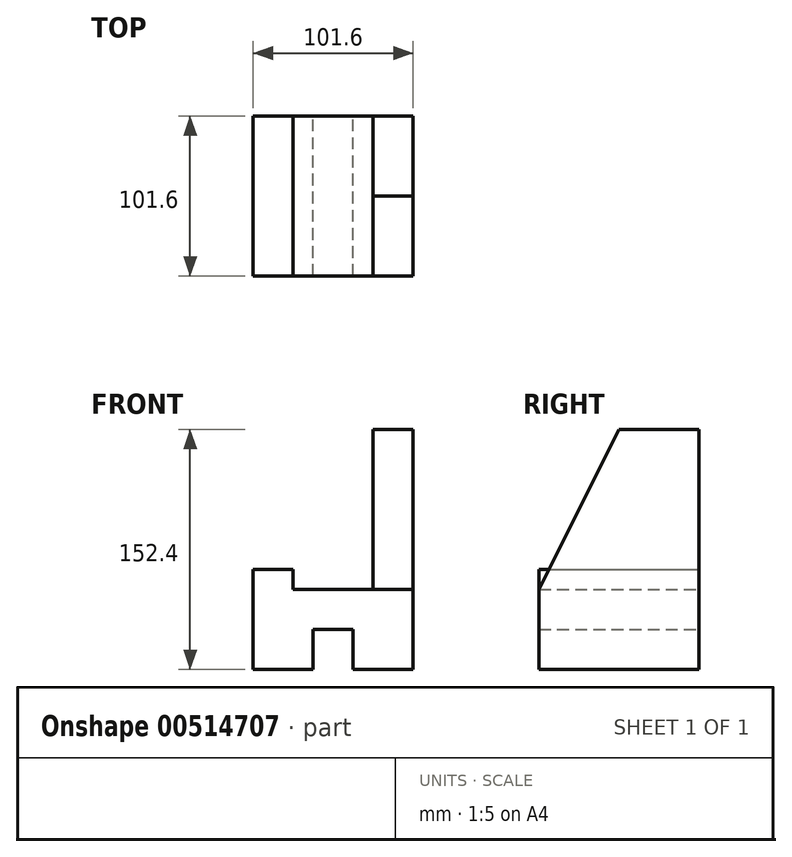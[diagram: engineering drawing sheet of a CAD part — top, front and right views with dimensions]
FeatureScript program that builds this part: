
annotation { "Feature Type Name" : "Feature", "Feature Type Description" : "" }
export const myFeature = defineFeature(function(context is Context, id is Id, definition is map)
    precondition{}
    {
        {
            var Q0;
            Q0=qCreatedBy(makeId("Front.planeOp"),FACE);
            var sketch = newSketch(context, id + "F0", { "sketchPlane" : qUnion([Q0])});
            skLineSegment(sketch, "E0", {"start": v(0, 0) * mm, "end": v(-76.2, 0) * mm});
            skLineSegment(sketch, "E1", {"start": v(-76.2, 0) * mm, "end": v(-76.2, 12.7) * mm});
            skLineSegment(sketch, "E2", {"start": v(-76.2, 12.7) * mm, "end": v(-101.6, 12.7) * mm});
            skLineSegment(sketch, "E3", {"start": v(-101.6, 12.7) * mm, "end": v(-101.6, -50.8) * mm});
            skLineSegment(sketch, "E4", {"start": v(-101.6, -50.8) * mm, "end": v(-63.5, -50.8) * mm});
            skLineSegment(sketch, "E5", {"start": v(-63.5, -50.8) * mm, "end": v(-63.5, -25.4) * mm});
            skLineSegment(sketch, "E6", {"start": v(-63.5, -25.4) * mm, "end": v(-38.1, -25.4) * mm});
            skLineSegment(sketch, "E7", {"start": v(-38.1, -25.4) * mm, "end": v(-38.1, -50.8) * mm});
            skLineSegment(sketch, "E8", {"start": v(-38.1, -50.8) * mm, "end": v(0, -50.8) * mm});
            skLineSegment(sketch, "E9", {"start": v(0, -50.8) * mm, "end": v(0, 0) * mm});
            skLineSegment(sketch, "E10", {"start": v(0, 0) * mm, "end": v(0, 101.6) * mm});
            skLineSegment(sketch, "E11", {"start": v(0, 101.6) * mm, "end": v(-25.4, 101.6) * mm});
            skLineSegment(sketch, "E12", {"start": v(-25.4, 101.6) * mm, "end": v(-25.4, 0) * mm});
            skSolve(sketch);
        }
        {
            var Q0;
            {var subQ3=sQuery(id+"F0.wireOp",EDGE,"E1");Q0=makeQuery(id+"F0.imprint","IMPRINT",FACE,{"disambiguationData":[TD([[makeQuery(id+"F0.imprint","IMPRINT",EDGE,{"derivedFrom":subQ3}),1.0]])]});}
            var Q1;
            {var subQ0=sQuery(id+"F0.wireOp",EDGE,"E10");Q1=makeQuery(id+"F0.imprint","IMPRINT",FACE,{"disambiguationData":[TD([[makeQuery(id+"F0.imprint","IMPRINT",EDGE,{"derivedFrom":subQ0}),1.0]])]});}
            extrude(context, id + "F1", {"entities" : qUnion([Q0, Q1]), "depth" : 101.6 * mm, "offsetDistance" : 25.4 * mm});
        }
        {
            var Q0;
            Q0=makeQuery(id+"F1.opExtrude","SWEPT_FACE",FACE,{"disambiguationData":[OSD([sQuery(id+"F0.wireOp",EDGE,"E9"),sQuery(id+"F0.wireOp",EDGE,"E10")])]});
            var sketch = newSketch(context, id + "F2", { "sketchPlane" : qUnion([Q0])});
            skLineSegment(sketch, "E13", {"start": v(0, -50.8) * mm, "end": v(-50.8, -50.8) * mm});
            skLineSegment(sketch, "E14", {"start": v(-101.6, -50.8) * mm, "end": v(-101.6, 0) * mm});
            skLineSegment(sketch, "E15", {"start": v(-101.6, 0) * mm, "end": v(-50.8, 101.6) * mm});
            skSolve(sketch);
        }
        {
            var Q0;
            {var subQ0=sQuery(id+"F2.wireOp",EDGE,"E15");Q0=makeQuery(id+"F2.imprint","IMPRINT",FACE,{"disambiguationData":[TD([[makeQuery(id+"F2.imprint","IMPRINT",EDGE,{"derivedFrom":subQ0}),1.0]])]});}
            extrude(context, id + "F3", {"entities" : qUnion([Q0]), "operationType" : NewBodyOperationType.REMOVE, "oppositeDirection" : true, "depth" : 25.4 * mm, "offsetDistance" : 25.4 * mm});
        }
    });
